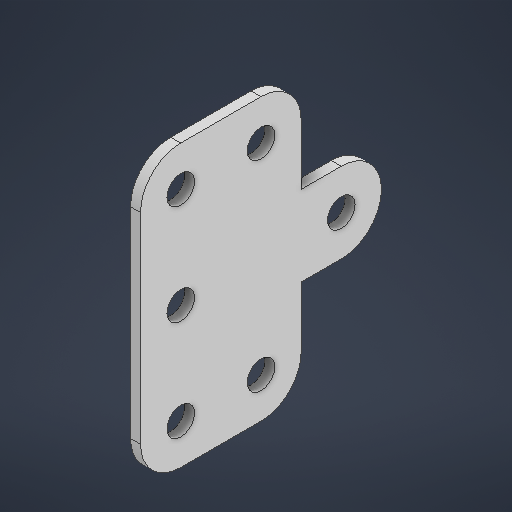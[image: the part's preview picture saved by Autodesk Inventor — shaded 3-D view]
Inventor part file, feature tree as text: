
AUTODESK INVENTOR PART (.ipt)
format: ipt  version: 2025.2 (Build 292293000, 293)  size: 219,648 bytes
history: native  units: in
note: dims shown in document units (in); Inventor stores cm internally (conversion verified against a paired STEP export)
features: extrude x1, sketch x1
ambient origin geometry x8: Origin, YZ Plane, XZ Plane, XY Plane, X Axis, Y Axis, Z Axis, Center Point
bodies: Solid1 (feature_tree)
feature tree (2):
  extrude  "Extrusion1"  Depth=0.25in
  sketch  "Sketch1"  dims[d16=0.0625in d17=0.0in d22=0.172in d23=0.172in d25=0.172in d27=0.172in d28=0.25in]
